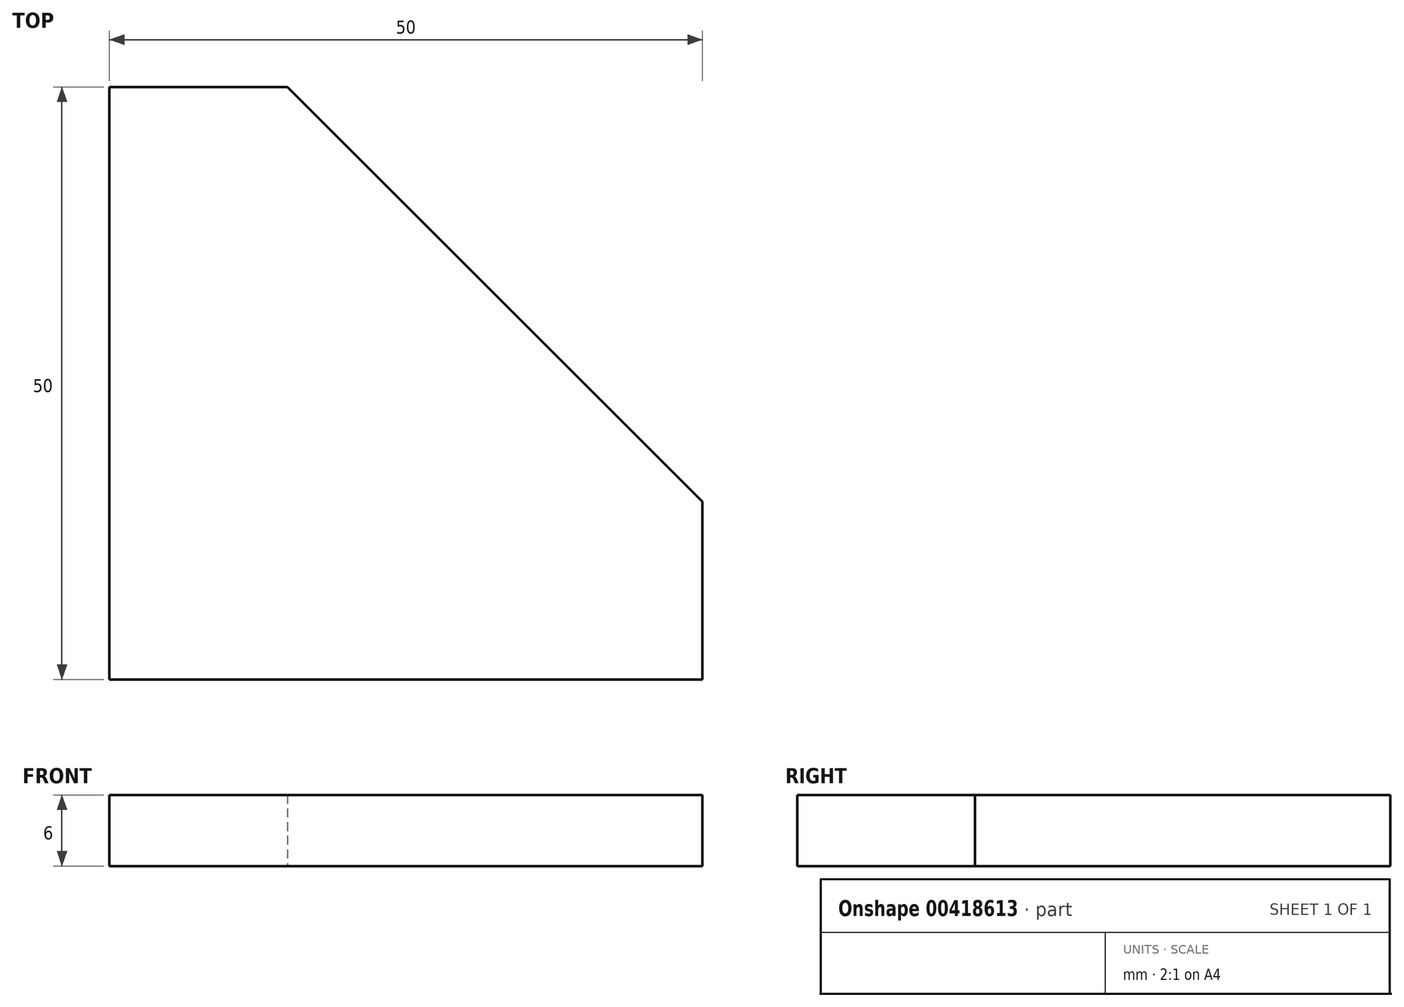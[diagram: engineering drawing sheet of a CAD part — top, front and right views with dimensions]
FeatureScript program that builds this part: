
annotation { "Feature Type Name" : "Feature", "Feature Type Description" : "" }
export const myFeature = defineFeature(function(context is Context, id is Id, definition is map)
    precondition{}
    {
        {
            var Q0;
            Q0=qCreatedBy(makeId("Top.planeOp"),FACE);
            var sketch = newSketch(context, id + "F0", { "sketchPlane" : qUnion([Q0])});
            skLineSegment(sketch, "E0", {"start": v(-40.95, 1.9) * mm, "end": v(-40.95, -48.1) * mm});
            skLineSegment(sketch, "E1", {"start": v(9.05, -48.1) * mm, "end": v(-40.95, -48.1) * mm});
            skLineSegment(sketch, "E2", {"start": v(-40.95, 1.9) * mm, "end": v(9.05, -48.1) * mm});
            skLineSegment(sketch, "E3", {"start": v(-40.95, 1.9) * mm, "end": v(-25.95, 1.91) * mm});
            skLineSegment(sketch, "E4", {"start": v(9.05, -48.1) * mm, "end": v(9.04, -33.1) * mm});
            skLineSegment(sketch, "E5", {"start": v(-25.95, 1.91) * mm, "end": v(9.04, -33.1) * mm});
            skLineSegment(sketch, "E6", {"start": v(-25.95, 1.91) * mm, "end": v(-33.46, -5.6) * mm});
            skSolve(sketch);
        }
        {
            var Q0;
            Q0 = qSketchRegion(id + "F0", true);
            extrude(context, id + "F1", {"entities" : qUnion([Q0]), "depth" : 6 * mm});
        }
    });
